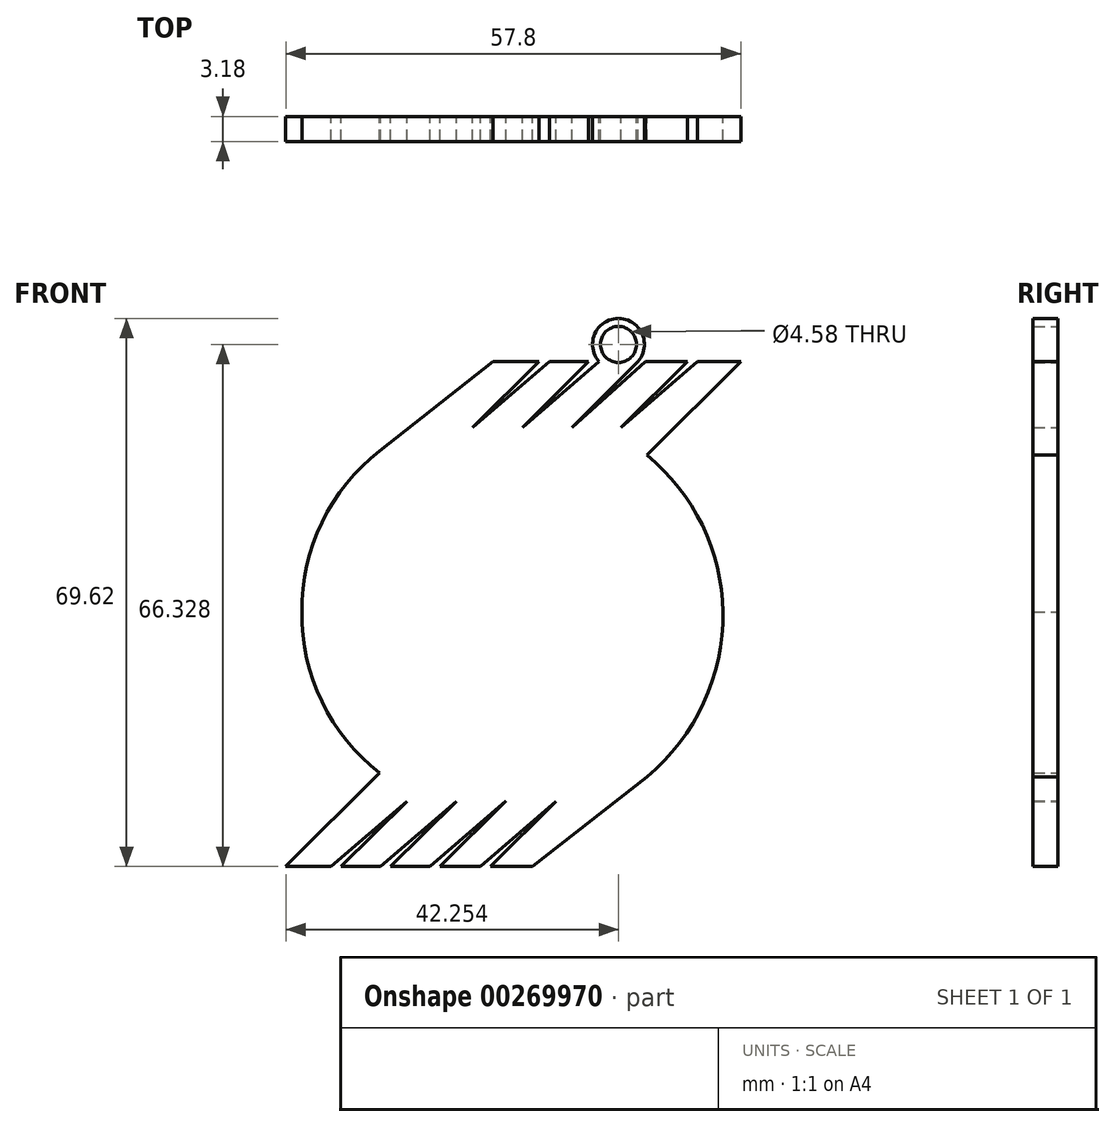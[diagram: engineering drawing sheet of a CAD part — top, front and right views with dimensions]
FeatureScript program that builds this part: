
annotation { "Feature Type Name" : "Feature", "Feature Type Description" : "" }
export const myFeature = defineFeature(function(context is Context, id is Id, definition is map)
    precondition{}
    {
        {
            var Q0;
            Q0=qCreatedBy(makeId("Front.planeOp"),FACE);
            var sketch = newSketch(context, id + "F0", { "sketchPlane" : qUnion([Q0])});
            skLineSegment(sketch, "E0", {"start": v(-3.4, 27.42) * mm, "end": v(2.43, 27.42) * mm});
            skLineSegment(sketch, "E1", {"start": v(2.43, 27.42) * mm, "end": v(-5.97, 19.05) * mm});
            skLineSegment(sketch, "E2", {"start": v(-5.97, 19.05) * mm, "end": v(3.76, 27.42) * mm});
            skLineSegment(sketch, "E3", {"start": v(3.76, 27.42) * mm, "end": v(8.76, 27.42) * mm});
            skLineSegment(sketch, "E4", {"start": v(8.76, 27.42) * mm, "end": v(0.35, 19.05) * mm});
            skLineSegment(sketch, "E5", {"start": v(0.35, 19.05) * mm, "end": v(10.04, 27.42) * mm});
            skLineSegment(sketch, "E6", {"start": v(10.04, 27.42) * mm, "end": v(10.08, 27.42) * mm});
            skLineSegment(sketch, "E7", {"start": v(15.05, 27.42) * mm, "end": v(6.65, 19.05) * mm});
            skLineSegment(sketch, "E8", {"start": v(6.65, 19.05) * mm, "end": v(15.98, 27.42) * mm});
            skLineSegment(sketch, "E9", {"start": v(15.98, 27.42) * mm, "end": v(21.28, 27.42) * mm});
            skLineSegment(sketch, "E10", {"start": v(21.28, 27.42) * mm, "end": v(12.87, 19.05) * mm});
            skLineSegment(sketch, "E11", {"start": v(12.87, 19.05) * mm, "end": v(22.58, 27.42) * mm});
            skLineSegment(sketch, "E12", {"start": v(22.58, 27.42) * mm, "end": v(28.1, 27.42) * mm});
            skLineSegment(sketch, "E13", {"start": v(28.1, 27.42) * mm, "end": v(16.16, 15.54) * mm});
            skLineSegment(sketch, "E14", {"start": v(-29.71, -36.72) * mm, "end": v(-17.82, -24.84) * mm});
            skLineSegment(sketch, "E15", {"start": v(-29.71, -36.72) * mm, "end": v(-23.96, -36.72) * mm});
            skLineSegment(sketch, "E16", {"start": v(-23.96, -36.72) * mm, "end": v(-14.34, -28.42) * mm});
            skLineSegment(sketch, "E17", {"start": v(-14.34, -28.42) * mm, "end": v(-22.71, -36.72) * mm});
            skLineSegment(sketch, "E18", {"start": v(-22.71, -36.72) * mm, "end": v(-17.66, -36.72) * mm});
            skLineSegment(sketch, "E19", {"start": v(-17.66, -36.72) * mm, "end": v(-8.06, -28.42) * mm});
            skLineSegment(sketch, "E20", {"start": v(-8.06, -28.42) * mm, "end": v(-16.42, -36.72) * mm});
            skLineSegment(sketch, "E21", {"start": v(-16.42, -36.72) * mm, "end": v(-11.37, -36.72) * mm});
            skLineSegment(sketch, "E22", {"start": v(-11.37, -36.72) * mm, "end": v(-1.73, -28.38) * mm});
            skLineSegment(sketch, "E23", {"start": v(-1.73, -28.38) * mm, "end": v(-10.13, -36.72) * mm});
            skLineSegment(sketch, "E24", {"start": v(-10.13, -36.72) * mm, "end": v(-4.96, -36.72) * mm});
            skLineSegment(sketch, "E25", {"start": v(-4.96, -36.72) * mm, "end": v(4.63, -28.42) * mm});
            skLineSegment(sketch, "E26", {"start": v(4.63, -28.42) * mm, "end": v(-3.73, -36.72) * mm});
            skLineSegment(sketch, "E27", {"start": v(-3.73, -36.72) * mm, "end": v(1.6, -36.72) * mm});
            skArc(sketch, "E28", {"start": v(-27.67, -4.39) * mm, "mid": v(-25.14, -15.77) * mm, "end": v(-17.82, -24.84) * mm});
            skArc(sketch, "E29", {"start": v(-17.82, 16.08) * mm, "mid": v(-25.14, 7) * mm, "end": v(-27.67, -4.39) * mm});
            skArc(sketch, "E30", {"start": v(25.8, -4.39) * mm, "mid": v(23.18, 6.64) * mm, "end": v(16.16, 15.54) * mm});
            skArc(sketch, "E31", {"start": v(16.16, -25.32) * mm, "mid": v(23.36, -15.95) * mm, "end": v(25.8, -4.39) * mm});
            skLineSegment(sketch, "E32", {"start": v(1.6, -36.72) * mm, "end": v(16.16, -25.32) * mm});
            skLineSegment(sketch, "E33", {"start": v(-17.82, 16.08) * mm, "end": v(-3.4, 27.42) * mm});
            skPoint(sketch, "E34.endSnap0", {"position": v(12.54, 27.42) * mm});
            skArc(sketch, "E35", {"start": v(15, 27.42) * mm, "mid": v(12.54, 32.9) * mm, "end": v(10.08, 27.42) * mm});
            skCircle(sketch, "E36", {"center": v(12.54, 29.6) * mm, "radius": 2.3 * mm});
            skLineSegment(sketch, "E37.trimOffspring", {"start": v(15, 27.42) * mm, "end": v(15.05, 27.42) * mm});
            skPoint(sketch, "E38.orphan", {"position": v(12.54, 26.58) * mm});
            skSolve(sketch);
        }
        {
            var Q0;
            Q0=makeQuery(id+"F0.imprint","IMPRINT",FACE,{"disambiguationData":[TD([[makeQuery(id+"F0.imprint","IMPRINT",EDGE,{"derivedFrom":sQuery(id+"F0.wireOp",EDGE,"E0")}),-1.0]])]});
            extrude(context, id + "F1", {"entities" : qUnion([Q0]), "depth" : 3.17 * mm});
        }
    });
